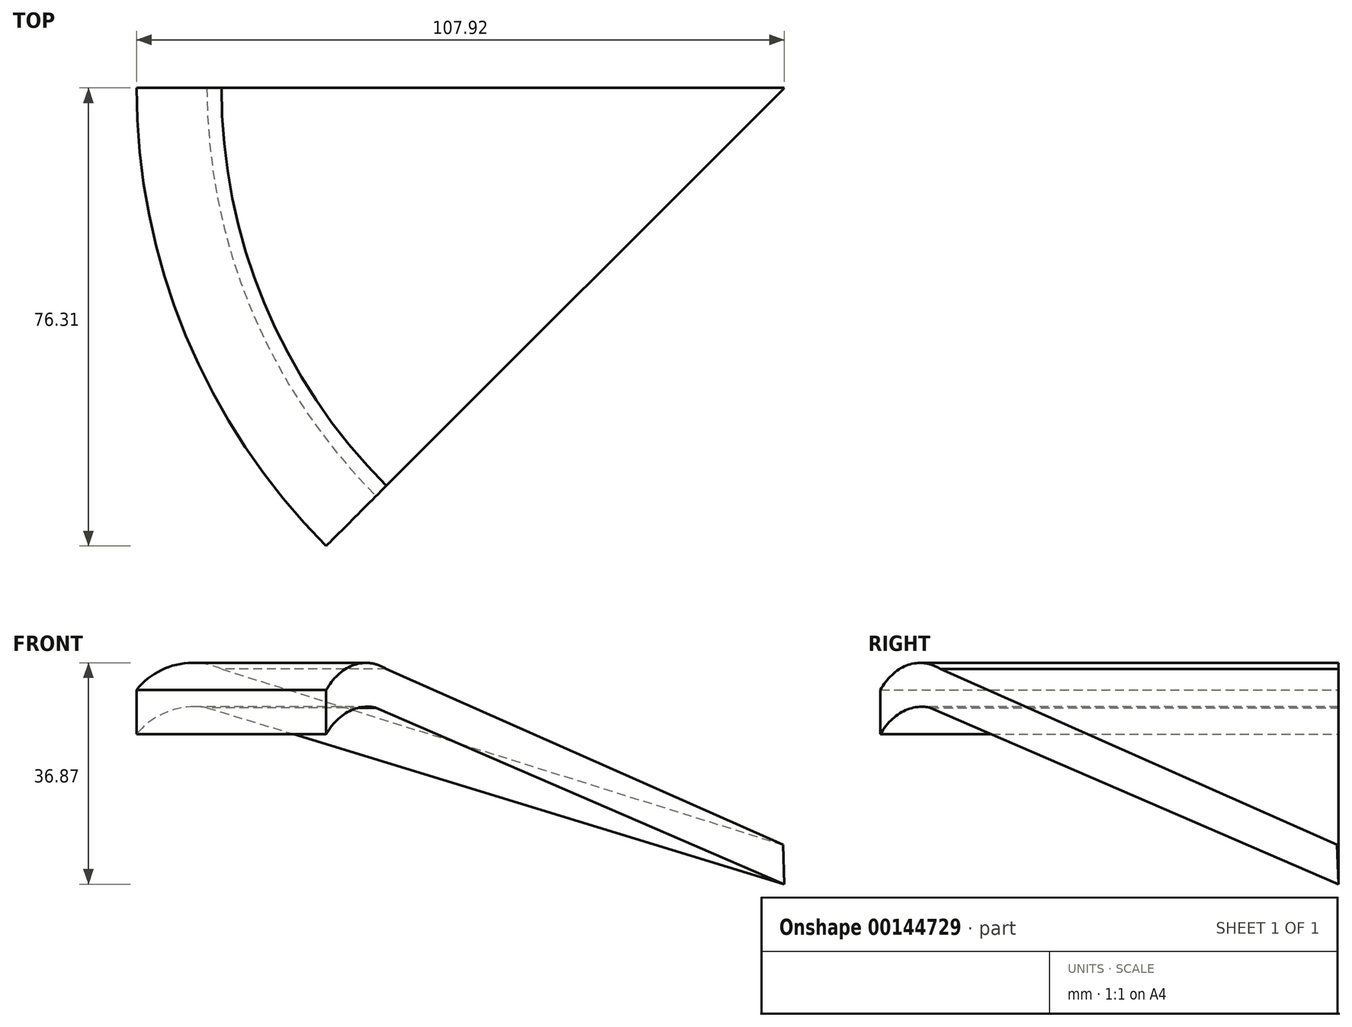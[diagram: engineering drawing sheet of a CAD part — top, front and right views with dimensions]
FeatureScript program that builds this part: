
annotation { "Feature Type Name" : "Feature", "Feature Type Description" : "" }
export const myFeature = defineFeature(function(context is Context, id is Id, definition is map)
    precondition{}
    {
        {
            var Q0;
            Q0=qCreatedBy(makeId("Front.planeOp"),FACE);
            var sketch = newSketch(context, id + "F0", { "sketchPlane" : qUnion([Q0])});
            skLineSegment(sketch, "E0", {"start": v(-0.32, 6.6) * mm, "end": v(0, 0) * mm});
            skLineSegment(sketch, "E1", {"start": v(0, 9.07) * mm, "end": v(0, 12.63) * mm});
            skLineSegment(sketch, "E2", {"start": v(0, 12.63) * mm, "end": v(0, 106.96) * mm});
            skLineSegment(sketch, "E3", {"start": v(0, 12.63) * mm, "end": v(-13.56, 12.63) * mm});
            skLineSegment(sketch, "E4", {"start": v(-13.56, 12.63) * mm, "end": v(-13.56, 52.33) * mm});
            skLineSegment(sketch, "E5", {"start": v(-13.56, 52.33) * mm, "end": v(0, 52.33) * mm});
            skArc(sketch, "E6", {"start": v(-96.18, 29.4) * mm, "mid": v(-102.64, 28.76) * mm, "end": v(-107.92, 25) * mm});
            skArc(sketch, "E7", {"start": v(-93.75, 35.85) * mm, "mid": v(-101.44, 36.52) * mm, "end": v(-107.92, 32.34) * mm});
            skLineSegment(sketch, "E8", {"start": v(-107.92, 25) * mm, "end": v(-107.92, 32.34) * mm});
            skLineSegment(sketch, "E9", {"start": v(-93.75, 35.85) * mm, "end": v(-0.32, 6.6) * mm});
            skLineSegment(sketch, "E10", {"start": v(-96.18, 29.4) * mm, "end": v(0, 0) * mm});
            skSolve(sketch);
        }
        {
            var Q0;
            Q0=makeQuery(id+"F0.imprint","IMPRINT",FACE,{"disambiguationData":[TD([[makeQuery(id+"F0.imprint","IMPRINT",EDGE,{"derivedFrom":sQuery(id+"F0.wireOp",EDGE,"qwOLyhjh-BWLk-kJDa-Hozp-orzQwl0dv6Qw")}),1.0]])]});
            var Q1;
            Q1=makeQuery(id+"F0.imprint","IMPRINT",FACE,{"disambiguationData":[TD([[makeQuery(id+"F0.imprint","IMPRINT",EDGE,{"derivedFrom":sQuery(id+"F0.wireOp",EDGE,"6a613768-63f5-4cfc-baf6-3e7752c35b4c.0")}),-1.0]])]});
            var Q2;
            Q2=makeQuery(id+"F0.imprint","IMPRINT",FACE,{"disambiguationData":[TD([[makeQuery(id+"F0.imprint","IMPRINT",EDGE,{"derivedFrom":sQuery(id+"F0.wireOp",EDGE,"E0")}),-1.0]])]});
            var Q3;
            Q3=sQuery(id+"F0.wireOp",EDGE,"E2");
            revolve(context, id + "F1", {"entities" : qUnion([Q0, Q1, Q2]), "axis" : qUnion([Q3]), "revolveType" : RevolveType.ONE_DIRECTION, "angle" : 45 * degree});
        }
    });
